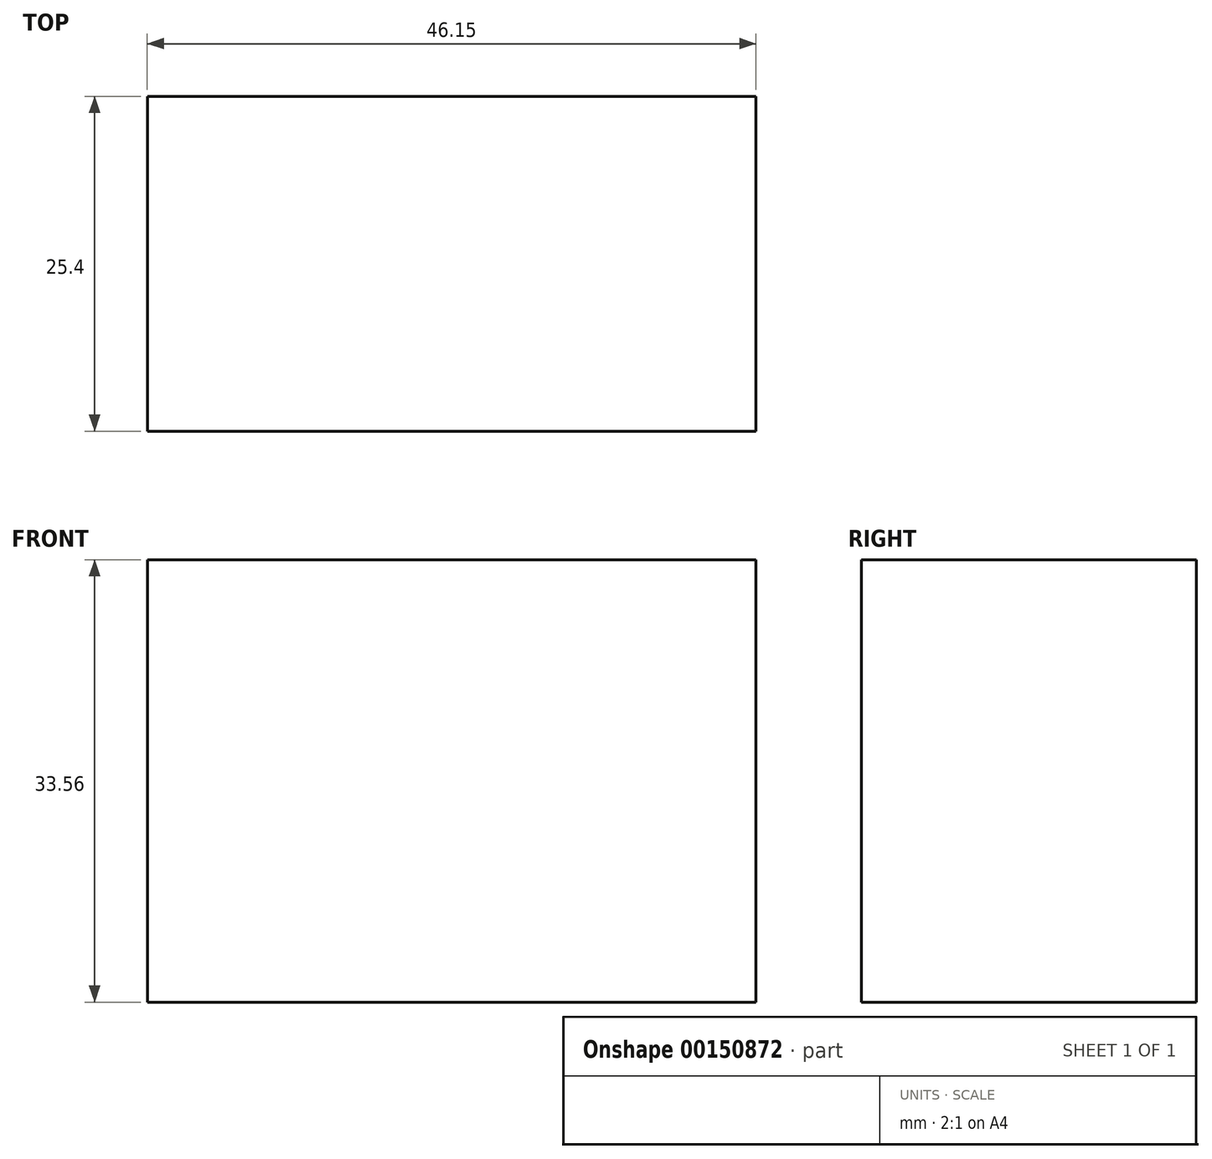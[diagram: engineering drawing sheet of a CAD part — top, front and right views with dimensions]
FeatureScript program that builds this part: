
annotation { "Feature Type Name" : "Feature", "Feature Type Description" : "" }
export const myFeature = defineFeature(function(context is Context, id is Id, definition is map)
    precondition{}
    {
        {
            var Q0;
            Q0=qCreatedBy(makeId("Front.planeOp"),FACE);
            var sketch = newSketch(context, id + "F0", { "sketchPlane" : qUnion([Q0])});
            skLineSegment(sketch, "E0.bottom", {"start": v(61.18, -19.75) * mm, "end": v(-61.18, -19.75) * mm});
            skLineSegment(sketch, "E0.top", {"start": v(61.18, 19.75) * mm, "end": v(-61.18, 19.75) * mm});
            skLineSegment(sketch, "E0.left", {"start": v(61.18, -19.75) * mm, "end": v(61.18, 19.75) * mm});
            skLineSegment(sketch, "E0.right", {"start": v(-61.18, -19.75) * mm, "end": v(-61.18, 19.75) * mm});
            skPoint(sketch, "E0.middle", {"position": v(0, 0) * mm});
            skLineSegment(sketch, "E1.bottom", {"start": v(141.07, 90.55) * mm, "end": v(94.92, 90.55) * mm});
            skLineSegment(sketch, "E1.top", {"start": v(141.07, 56.99) * mm, "end": v(94.92, 56.99) * mm});
            skLineSegment(sketch, "E1.left", {"start": v(141.07, 90.55) * mm, "end": v(141.07, 56.99) * mm});
            skLineSegment(sketch, "E1.right", {"start": v(94.92, 90.55) * mm, "end": v(94.92, 56.99) * mm});
            skLineSegment(sketch, "E2", {"start": v(61.18, 19.75) * mm, "end": v(61.18, 44.4) * mm});
            skArc(sketch, "E3", {"start": v(61.18, 44.4) * mm, "mid": v(65.82, 52.72) * mm, "end": v(75.34, 53.14) * mm});
            skSolve(sketch);
        }
        {
            var Q0;
            Q0=makeQuery(id+"F0.imprint","IMPRINT",FACE,{"disambiguationData":[TD([[makeQuery(id+"F0.imprint","IMPRINT",EDGE,{"derivedFrom":sQuery(id+"F0.wireOp",EDGE,"E1.bottom")}),1.0]])]});
            extrude(context, id + "F1", {"entities" : qUnion([Q0]), "depth" : 25.4 * mm});
        }
    });
